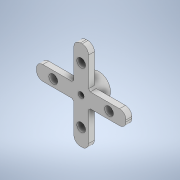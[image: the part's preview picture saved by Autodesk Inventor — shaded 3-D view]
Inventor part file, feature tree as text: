
AUTODESK INVENTOR PART (.ipt)
format: ipt  version: 2020 (Build 240168000, 168)  size: 368,640 bytes
history: native  units: in
note: dims shown in document units (in); Inventor stores cm internally (conversion verified against a paired STEP export)
features: extrude x3, sketch x3, fillet x1
ambient origin geometry x8: Origin, YZ Plane, XZ Plane, XY Plane, X Axis, Y Axis, Z Axis, Center Point
bodies: Solid1 (feature_tree)
feature tree (7):
  extrude  "Extrusion1"  Depth=0.1614in
  extrude  "Extrusion2"  Depth=0.0787in
  extrude  "Extrusion3"  Depth=0.1969in
  fillet  "Fillet1"  Radius=0.4537in
  sketch  "Sketch2"  dims[d7=0.315in d8=0.1614in]
  sketch  "Sketch3"  dims[d14=0.1575in d15=0.0in d16=0.0787in]
  sketch  "Sketch4"  dims[d17=0.0787in d18=0.0in d20=0.1969in d21=0.4537in d22=0.0243in d23=0.1969in d24=1.5748in d26=360.0deg d28=0.0787in d29=0.0in d30=0.0866in d31=0.1181in d32=1.5748in d34=360.0deg d36=0.1969in]
